# Revit family: Skylight-Wasco-SS-Sentinel_Fall_Protection
name_source: partatom
category: Windows
revit_build: Autodesk Revit Architecture 2013 (Build: 20130531_2115(x64)
units: mm (PartAtom-declared; Revit-internal decimal feet)

## types (18) — shared parameters
12in Curb Height = No
4in Curb Height = Yes
9in Curb Height = No
Acrylic Glazing Inner = Acrylic - Wasco - Clear
Acrylic Glazing Outer = Acrylic - Wasco - Clear
Curb = Aluminum - Wasco - Aged Copper
Curb Height = 0' - 4"
Curb Width = 0' - 1 1/2"
Default Elevation = 0' - 0"
Description = Skylight
Finish = Aluminum - Wasco - Aged Copper
Host Constraint = 1
Manufacturer = Wasco
Overhang = 0' - 1 25/32"
Product Documentation Link = http://www.wascoskylights.com
Product Name = SS Sentinel Fall Protection
Product Page URL = http://www.wascoskylights.com
Type Comments = Maximum length and width = 78in x 78in.  Long leg to short leg maximum ratio cannot be more than 2.3.
URL = http://www.wascoskylights.com

## per-type parameters (varying)
| type | Height | Host Length | Host Width | L | Length | R | Rough Height | Rough Length | Rough Width | S | Width |
| DDSS2424 | 0' - 1 15/16" | 3' - 10" | 3' - 10" | 0' - 9 29/32" | 1' - 10" | 2' - 2 13/32" | 0' - 6 15/32" | 1' - 11 25/32" | 1' - 11 25/32" | 0' - 1 15/16" | 1' - 10" |
| DDSS2828 | 0' - 2 1/4" | 4' - 1 1/4" | 4' - 1 1/4" | 0' - 11 17/32" | 2' - 1 1/4" | 2' - 6 3/4" | 0' - 6 25/32" | 2' - 3 1/32" | 2' - 3 1/32" | 0' - 2 1/4" | 2' - 1 1/4" |
| DDSS2836 | 0' - 2 1/4" | 4' - 9 1/4" | 4' - 1 1/4" | 0' - 11 17/32" | 2' - 9 1/4" | 2' - 6 3/4" | 0' - 6 25/32" | 2' - 11 1/32" | 2' - 3 1/32" | 0' - 2 1/4" | 2' - 1 1/4" |
| DDSS2852 | 0' - 2 1/4" | 6' - 1 1/4" | 4' - 1 1/4" | 0' - 11 17/32" | 4' - 1 1/4" | 2' - 6 3/4" | 0' - 6 25/32" | 4' - 3 1/32" | 2' - 3 1/32" | 0' - 2 1/4" | 2' - 1 1/4" |
| DDSS3636 | 0' - 3 1/32" | 4' - 9 1/4" | 4' - 9 1/4" | 1' - 3 17/32" | 2' - 9 1/4" | 3' - 5 13/32" | 0' - 7 9/16" | 2' - 11 1/32" | 2' - 11 1/32" | 0' - 3 1/32" | 2' - 9 1/4" |
| DDSS3652 | 0' - 3 1/32" | 6' - 0 1/4" | 4' - 9 1/4" | 1' - 3 17/32" | 4' - 0 1/4" | 3' - 5 13/32" | 0' - 7 9/16" | 4' - 2 1/32" | 2' - 11 1/32" | 0' - 3 1/32" | 2' - 9 1/4" |
| DDSS3676 | 0' - 3 1/32" | 8' - 0 1/2" | 4' - 9 1/4" | 1' - 3 17/32" | 6' - 0 1/2" | 3' - 5 13/32" | 0' - 7 9/16" | 6' - 2 9/32" | 2' - 11 1/32" | 0' - 3 1/32" | 2' - 9 1/4" |
| DDSS4242 | 0' - 3 11/16" | 5' - 4" | 5' - 4" | 1' - 6 29/32" | 3' - 4" | 4' - 2 13/32" | 0' - 8 7/32" | 3' - 5 25/32" | 3' - 5 25/32" | 0' - 3 11/16" | 3' - 4" |
| DDSS4280 | 0' - 3 11/16" | 8' - 6" | 5' - 4" | 1' - 6 29/32" | 6' - 6" | 4' - 2 13/32" | 0' - 8 7/32" | 6' - 7 25/32" | 3' - 5 25/32" | 0' - 3 11/16" | 3' - 4" |
| DDSS5252 | 0' - 4 19/32" | 6' - 1 1/4" | 6' - 1 1/4" | 1' - 11 17/32" | 4' - 1 1/4" | 5' - 2 3/4" | 0' - 9 1/8" | 4' - 3 1/32" | 4' - 3 1/32" | 0' - 4 19/32" | 4' - 1 1/4" |
| DDSS5276 | 0' - 4 19/32" | 8' - 0 1/2" | 6' - 1 1/4" | 1' - 11 17/32" | 6' - 0 1/2" | 5' - 2 3/4" | 0' - 9 1/8" | 6' - 2 9/32" | 4' - 3 1/32" | 0' - 4 19/32" | 4' - 1 1/4" |
| DDSS5296 | 0' - 4 19/32" | 9' - 8 1/2" | 6' - 1 1/4" | 1' - 11 17/32" | 7' - 8 1/2" | 5' - 2 3/4" | 0' - 9 1/8" | 7' - 10 9/32" | 4' - 3 1/32" | 0' - 4 19/32" | 4' - 1 1/4" |
| DDSS6060 | 0' - 5 7/16" | 6' - 10" | 6' - 10" | 2' - 3 29/32" | 4' - 10" | 6' - 2 13/32" | 0' - 9 31/32" | 4' - 11 25/32" | 4' - 11 25/32" | 0' - 5 7/16" | 4' - 10" |
| DDSS6476 | 0' - 5 11/16" | 8' - 0 1/2" | 7' - 0 1/2" | 2' - 5 5/32" | 6' - 0 1/2" | 6' - 5 3/4" | 0' - 10 7/32" | 6' - 2 9/32" | 5' - 2 9/32" | 0' - 5 11/16" | 5' - 0 1/2" |
| DDSS6496 | 0' - 5 11/16" | 9' - 8 1/2" | 7' - 0 1/2" | 2' - 5 5/32" | 7' - 8 1/2" | 6' - 5 3/4" | 0' - 10 7/32" | 7' - 10 9/32" | 5' - 2 9/32" | 0' - 5 11/16" | 5' - 0 1/2" |
| DDSS7272 | 0' - 6 11/16" | 7' - 11" | 7' - 11" | 2' - 10 13/32" | 5' - 11" | 7' - 7 3/4" | 0' - 11 7/32" | 6' - 0 25/32" | 6' - 0 25/32" | 0' - 6 11/16" | 5' - 11" |
| DDSS8080 | 0' - 7 3/8" | 8' - 6" | 8' - 6" | 3' - 1 29/32" | 6' - 6" | 8' - 5 3/32" | 0' - 11 29/32" | 6' - 7 25/32" | 6' - 7 25/32" | 0' - 7 3/8" | 6' - 6" |
| Custom | 0' - 4 15/32" | 6' - 0" | 6' - 0" | 1' - 10 29/32" | 4' - 0" | 5' - 1 3/32" | 0' - 9" | 4' - 1 25/32" | 4' - 1 25/32" | 0' - 4 15/32" | 4' - 0" |

note: column(s) folded — value = type name in every type: Model

## geometry (parser evidence)
native form markers: Blend x18, Extrusion x1, Sweep x3
no freeform markers — native parametric forms only
